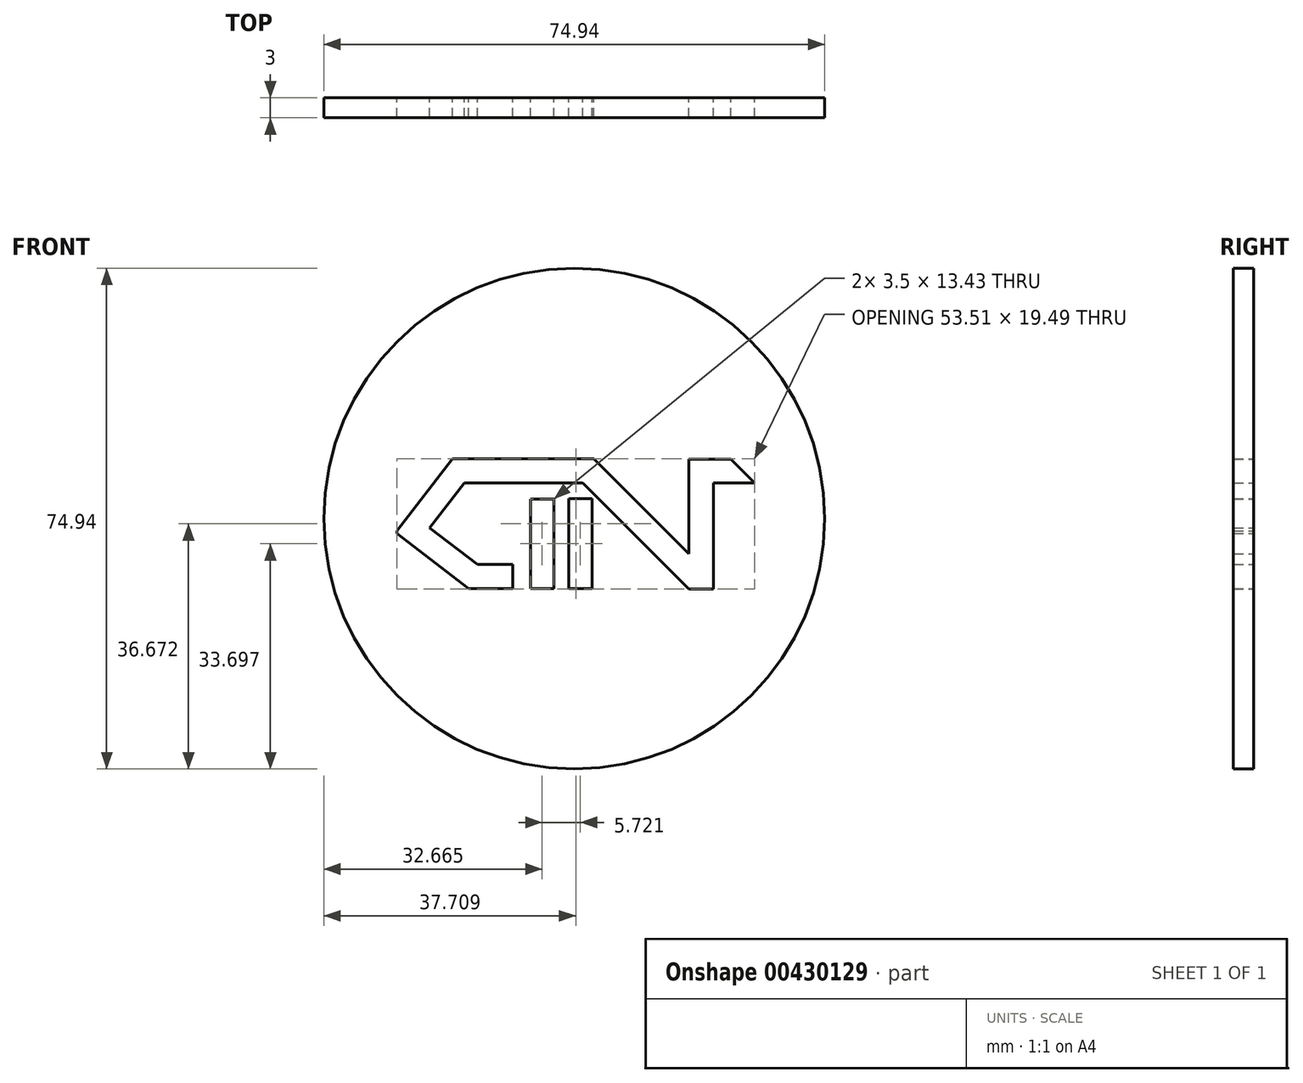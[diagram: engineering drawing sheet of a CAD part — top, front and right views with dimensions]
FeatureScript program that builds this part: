
annotation { "Feature Type Name" : "Feature", "Feature Type Description" : "" }
export const myFeature = defineFeature(function(context is Context, id is Id, definition is map)
    precondition{}
    {
        {
            var Q0;
            Q0=qCreatedBy(makeId("Front.planeOp"),FACE);
            var sketch = newSketch(context, id + "F0", { "sketchPlane" : qUnion([Q0])});
            skLineSegment(sketch, "E0", {"start": v(-9.22, -6.88) * mm, "end": v(-9.22, -10.46) * mm});
            skLineSegment(sketch, "E1", {"start": v(-9.22, -10.46) * mm, "end": v(-15.78, -10.46) * mm});
            skLineSegment(sketch, "E2", {"start": v(-15.78, -10.46) * mm, "end": v(-26.52, -2.26) * mm});
            skLineSegment(sketch, "E3", {"start": v(-26.52, -2.26) * mm, "end": v(-26.52, -1.86) * mm});
            skLineSegment(sketch, "E4", {"start": v(-26.52, -1.86) * mm, "end": v(-18.22, 8.95) * mm});
            skLineSegment(sketch, "E5", {"start": v(-18.22, 8.95) * mm, "end": v(2.89, 8.95) * mm});
            skLineSegment(sketch, "E6", {"start": v(2.89, 8.95) * mm, "end": v(17.13, -5.28) * mm});
            skLineSegment(sketch, "E7", {"start": v(17.13, -5.28) * mm, "end": v(17.13, 8.88) * mm});
            skLineSegment(sketch, "E8", {"start": v(17.13, 8.88) * mm, "end": v(23.45, 8.88) * mm});
            skLineSegment(sketch, "E9", {"start": v(23.45, 8.88) * mm, "end": v(27, 5.32) * mm});
            skLineSegment(sketch, "E10", {"start": v(27, 5.32) * mm, "end": v(20.82, 5.32) * mm});
            skLineSegment(sketch, "E11", {"start": v(20.82, 5.32) * mm, "end": v(20.82, -10.54) * mm});
            skLineSegment(sketch, "E12", {"start": v(20.82, -10.54) * mm, "end": v(17.13, -10.54) * mm});
            skLineSegment(sketch, "E13", {"start": v(17.13, -10.54) * mm, "end": v(1.24, 5.32) * mm});
            skLineSegment(sketch, "E14", {"start": v(1.24, 5.32) * mm, "end": v(-16.45, 5.32) * mm});
            skLineSegment(sketch, "E15", {"start": v(-16.45, 5.32) * mm, "end": v(-21.63, -1.41) * mm});
            skLineSegment(sketch, "E16", {"start": v(-21.63, -1.41) * mm, "end": v(-14.48, -6.88) * mm});
            skLineSegment(sketch, "E17", {"start": v(-14.48, -6.88) * mm, "end": v(-9.22, -6.88) * mm});
            skLineSegment(sketch, "E18", {"start": v(-6.56, -10.49) * mm, "end": v(-3.05, -10.49) * mm});
            skLineSegment(sketch, "E19", {"start": v(-3.05, -10.49) * mm, "end": v(-3.05, 2.94) * mm});
            skLineSegment(sketch, "E20", {"start": v(-3.05, 2.94) * mm, "end": v(-6.55, 2.94) * mm});
            skLineSegment(sketch, "E21", {"start": v(-6.55, 2.94) * mm, "end": v(-6.56, -10.49) * mm});
            skLineSegment(sketch, "E22", {"start": v(-0.83, -10.46) * mm, "end": v(2.67, -10.46) * mm});
            skLineSegment(sketch, "E23", {"start": v(2.67, -10.46) * mm, "end": v(2.67, 2.97) * mm});
            skLineSegment(sketch, "E24", {"start": v(2.67, 2.97) * mm, "end": v(-0.83, 2.97) * mm});
            skLineSegment(sketch, "E25", {"start": v(-0.83, 2.97) * mm, "end": v(-0.83, -10.46) * mm});
            skCircle(sketch, "E26", {"center": v(0, 0) * mm, "radius": 37.47 * mm});
            skSolve(sketch);
        }
        {
            var Q0;
            Q0 = qSketchRegion(id + "F0", true);
            extrude(context, id + "F1", {"entities" : qUnion([Q0]), "depth" : 3 * mm});
        }
    });
